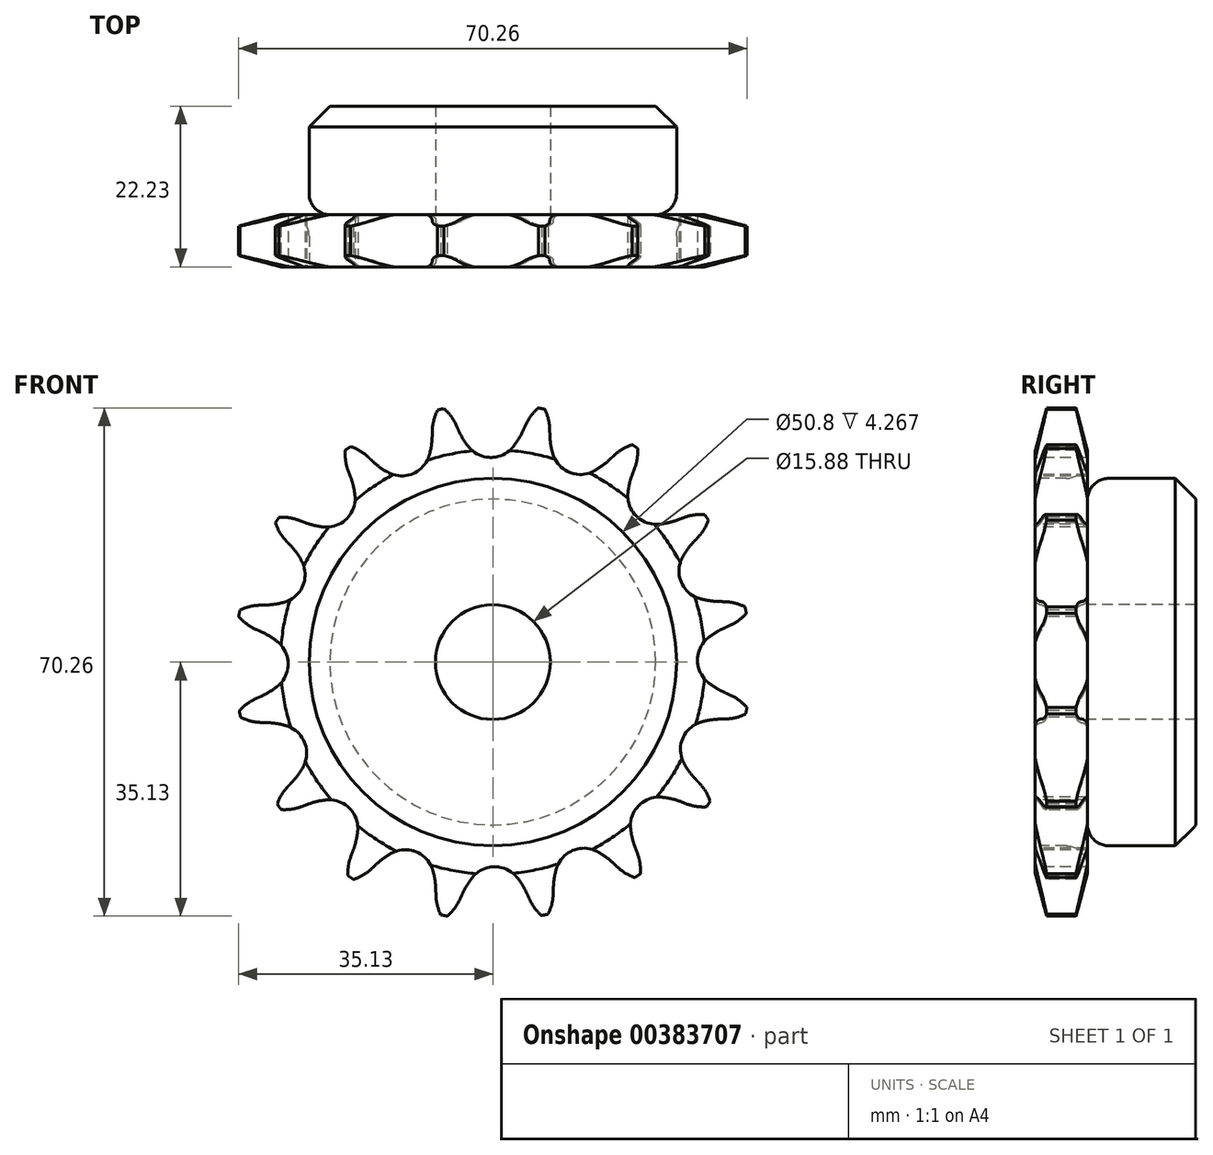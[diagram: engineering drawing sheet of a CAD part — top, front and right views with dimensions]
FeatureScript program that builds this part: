
annotation { "Feature Type Name" : "Feature", "Feature Type Description" : "" }
export const myFeature = defineFeature(function(context is Context, id is Id, definition is map)
    precondition{}
    {
        {
            var Q0;
            Q0=qCreatedBy(makeId("Right.planeOp"),FACE);
            var sketch = newSketch(context, id + "F0", { "sketchPlane" : qUnion([Q0])});
            skLineSegment(sketch, "E0", {"start": v(0, 0) * mm, "end": v(31.18, 0) * mm, "construction": true});
            skLineSegment(sketch, "E1.bottom", {"start": v(0, 7.94) * mm, "end": v(7.21, 7.94) * mm});
            skLineSegment(sketch, "E1.top", {"start": v(0, 35.69) * mm, "end": v(7.21, 35.69) * mm});
            skLineSegment(sketch, "E1.left", {"start": v(0, 7.94) * mm, "end": v(0, 35.69) * mm});
            skLineSegment(sketch, "E1.right", {"start": v(7.21, 7.94) * mm, "end": v(7.21, 35.69) * mm});
            skLineSegment(sketch, "E2.bottom", {"start": v(0, 7.94) * mm, "end": v(22.23, 7.94) * mm});
            skLineSegment(sketch, "E2.top", {"start": v(0, 25.4) * mm, "end": v(22.23, 25.4) * mm});
            skLineSegment(sketch, "E2.left", {"start": v(0, 7.94) * mm, "end": v(0, 25.4) * mm});
            skLineSegment(sketch, "E2.right", {"start": v(22.23, 7.94) * mm, "end": v(22.23, 25.4) * mm});
            skLineSegment(sketch, "E3.MirrorCS", {"start": v(7.21, -7.94) * mm, "end": v(7.21, -35.69) * mm});
            skLineSegment(sketch, "E4.MirrorCS", {"start": v(0, -7.94) * mm, "end": v(22.23, -7.94) * mm});
            skLineSegment(sketch, "E5.MirrorCS", {"start": v(0, -7.94) * mm, "end": v(0, -25.4) * mm});
            skLineSegment(sketch, "E6.MirrorCS", {"start": v(0, -7.94) * mm, "end": v(0, -35.69) * mm});
            skLineSegment(sketch, "E7.MirrorCS", {"start": v(22.23, -7.94) * mm, "end": v(22.23, -25.4) * mm});
            skLineSegment(sketch, "E8.MirrorCS", {"start": v(0, -25.4) * mm, "end": v(22.23, -25.4) * mm});
            skLineSegment(sketch, "E9.MirrorCS", {"start": v(0, -35.69) * mm, "end": v(7.21, -35.69) * mm});
            skSolve(sketch);
        }
        {
            var Q0;
            {var subQ5=sQuery(id+"F0.wireOp",EDGE,"E2.right");Q0=makeQuery(id+"F0.imprint","IMPRINT",FACE,{"disambiguationData":[TD([[makeQuery(id+"F0.imprint","IMPRINT",EDGE,{"derivedFrom":subQ5}),1.0]])]});}
            var Q1;
            {var subQ5=sQuery(id+"F0.wireOp",EDGE,"E2.left");Q1=makeQuery(id+"F0.imprint","IMPRINT",FACE,{"disambiguationData":[TD([[makeQuery(id+"F0.imprint","IMPRINT",EDGE,{"derivedFrom":subQ5}),-1.0]])]});}
            var Q2;
            {var subQ0=sQuery(id+"F0.wireOp",EDGE,"E1.top");Q2=makeQuery(id+"F0.imprint","IMPRINT",FACE,{"disambiguationData":[TD([[makeQuery(id+"F0.imprint","IMPRINT",EDGE,{"derivedFrom":subQ0}),-1.0]])]});}
            var Q3;
            Q3=sQuery(id+"F0.wireOp",EDGE,"E0");
            revolve(context, id + "F1", {"entities" : qUnion([Q0, Q1, Q2]), "axis" : qUnion([Q3]), "revolveType" : RevolveType.FULL});
        }
        {
            var Q0;
            Q0=makeQuery(id+"F1.opRevolve","SWEPT_EDGE",EDGE,{"disambiguationData":[OSD([sQuery(id+"F0.wireOp",EDGE,"E1.right"),sQuery(id+"F0.wireOp",EDGE,"E2.top")])]});
            fillet(context, id + "F2", {"entities" : qUnion([Q0]), "radius" : 2.95 * mm, "tangentPropagation" : true, "allowEdgeOverflow" : false});
        }
        {
            var Q0;
            Q0=makeQuery(id+"F1.opRevolve","SWEPT_EDGE",EDGE,{"disambiguationData":[OSD([sQuery(id+"F0.wireOp",EDGE,"E2.top"),sQuery(id+"F0.wireOp",EDGE,"E2.right")])]});
            chamfer(context, id + "F3", {"entities" : qUnion([Q0]), "width" : 2.87 * mm, "tangentPropagation" : true});
        }
        {
            var Q0;
            Q0=makeQuery(id+"F1.opRevolve","SWEPT_EDGE",EDGE,{"disambiguationData":[OSD([sQuery(id+"F0.wireOp",EDGE,"E1.top"),sQuery(id+"F0.wireOp",EDGE,"E1.left")])]});
            var Q1;
            Q1=makeQuery(id+"F1.opRevolve","SWEPT_FACE",FACE,{"disambiguationData":[OSD([sQuery(id+"F0.wireOp",EDGE,"E1.top")])]});
            chamfer(context, id + "F4", {"entities" : qUnion([Q0, Q1]), "chamferType" : ChamferType.TWO_OFFSETS, "width1" : 6.35 * mm, "oppositeDirection" : false, "width2" : 1.57 * mm, "tangentPropagation" : true});
        }
        {
            var Q0;
            Q0=qCreatedBy(makeId("Front.planeOp"),FACE);
            var sketch = newSketch(context, id + "F5", { "sketchPlane" : qUnion([Q0])});
            skCircle(sketch, "E10", {"center": v(0, -0.05) * mm, "radius": 32.55 * mm, "construction": true});
            skLineSegment(sketch, "E11", {"start": v(0, -0.05) * mm, "end": v(0, 32.5) * mm, "construction": true});
            skLineSegment(sketch, "E12", {"start": v(-32.56, -60.2) * mm, "end": v(-32.56, -60.2) * mm});
            skLineSegment(sketch, "E13", {"start": v(0, 32.5) * mm, "end": v(47.93, 32.5) * mm, "construction": true});
            skLineSegment(sketch, "E14", {"start": v(0, 32.5) * mm, "end": v(4.98, 36.5) * mm, "construction": true});
            skLineSegment(sketch, "E15", {"start": v(4.98, 36.5) * mm, "end": v(-4.46, 32.25) * mm, "construction": true});
            skLineSegment(sketch, "E16", {"start": v(-4.46, 32.25) * mm, "end": v(-4.46, 32.25) * mm});
            skLineSegment(sketch, "E17", {"start": v(0, -0.05) * mm, "end": v(-7.14, 35.8) * mm, "construction": true});
            skPoint(sketch, "E17.endSnap0", {"position": v(-6.06, 35.8) * mm});
            skLineSegment(sketch, "E18", {"start": v(-7.14, 35.8) * mm, "end": v(-7.14, 35.8) * mm});
            skLineSegment(sketch, "E19", {"start": v(-4.82, 33.05) * mm, "end": v(-4.82, 33.05) * mm});
            skArc(sketch, "E20", {"start": v(-4.5, 32.19) * mm, "mid": v(-4.65, 32.62) * mm, "end": v(-4.82, 33.05) * mm, "construction": true});
            skArc(sketch, "E21", {"start": v(-7.14, 35.8) * mm, "mid": v(-16.16, 26.46) * mm, "end": v(-4.5, 32.19) * mm, "construction": true});
            skArc(sketch, "E22", {"start": v(-10.19, 23.78) * mm, "mid": v(-5.13, 27.04) * mm, "end": v(-4.82, 33.05) * mm, "construction": true});
            skArc(sketch, "E23", {"start": v(-4.46, 32.25) * mm, "mid": v(-3.85, 31.1) * mm, "end": v(-3.1, 30.02) * mm});
            skLineSegment(sketch, "E24", {"start": v(-3.1, 30.02) * mm, "end": v(-3.1, 30.02) * mm});
            skLineSegment(sketch, "E25", {"start": v(-4.82, 33.05) * mm, "end": v(-7.66, 39.35) * mm, "construction": true});
            skLineSegment(sketch, "E26", {"start": v(-4.46, 32.25) * mm, "end": v(-4.82, 33.05) * mm, "construction": true});
            skLineSegment(sketch, "E27", {"start": v(-4.82, 33.05) * mm, "end": v(-4.46, 32.25) * mm});
            skArc(sketch, "E28.MirrorCS", {"start": v(4.45, 32.25) * mm, "mid": v(3.84, 31.1) * mm, "end": v(3.08, 30.02) * mm});
            skLineSegment(sketch, "E29.MirrorCS", {"start": v(4.45, 32.25) * mm, "end": v(4.8, 33.05) * mm});
            skArc(sketch, "E30", {"start": v(-3.1, 30.02) * mm, "mid": v(13.82, 41.92) * mm, "end": v(-4.46, 32.25) * mm, "construction": true});
            skArc(sketch, "E31", {"start": v(3.08, 30.02) * mm, "mid": v(0, 36.46) * mm, "end": v(-3.1, 30.02) * mm, "construction": true});
            skArc(sketch, "E32", {"start": v(-3.1, 30.02) * mm, "mid": v(0, 28.54) * mm, "end": v(3.08, 30.02) * mm});
            skArc(sketch, "E33", {"start": v(-4.82, 33.05) * mm, "mid": v(-5.79, 34.59) * mm, "end": v(-7.14, 35.8) * mm});
            skArc(sketch, "E34", {"start": v(-4.82, 33.05) * mm, "mid": v(-5.67, 34.43) * mm, "end": v(-6.82, 35.57) * mm});
            skArc(sketch, "E35", {"start": v(-6.82, 35.57) * mm, "mid": v(-6.98, 35.69) * mm, "end": v(-7.14, 35.8) * mm});
            skArc(sketch, "E36", {"start": v(-7.14, 35.8) * mm, "mid": v(-17.22, 31.96) * mm, "end": v(-10.19, 23.78) * mm, "construction": true});
            skArc(sketch, "E37.1.0", {"start": v(-27.44, -24.08) * mm, "mid": v(-19.07, -30.9) * mm, "end": v(-15.5, -20.71) * mm, "construction": true});
            skArc(sketch, "E37.1.1", {"start": v(-15.5, -20.71) * mm, "mid": v(-20.85, -17.96) * mm, "end": v(-26.2, -20.7) * mm, "construction": true});
            skArc(sketch, "E37.2.0", {"start": v(34.57, -11.72) * mm, "mid": v(36.3, -1.07) * mm, "end": v(25.7, -3.07) * mm, "construction": true});
            skArc(sketch, "E37.2.1", {"start": v(25.7, -3.07) * mm, "mid": v(25.98, -9.08) * mm, "end": v(31.03, -12.35) * mm, "construction": true});
            skPoint(sketch, "E37.center", {"position": v(0, 0) * mm});
            skArc(sketch, "E38.1.0", {"start": v(-26.2, -20.7) * mm, "mid": v(-26.99, -22.12) * mm, "end": v(-27.4, -23.7) * mm});
            skLineSegment(sketch, "E38.1.1", {"start": v(-26.2, -20.7) * mm, "end": v(-25.7, -20) * mm});
            skArc(sketch, "E38.1.2", {"start": v(-25.7, -20) * mm, "mid": v(-25, -18.88) * mm, "end": v(-24.45, -17.7) * mm});
            skArc(sketch, "E38.1.3", {"start": v(-24.45, -17.7) * mm, "mid": v(-24.71, -14.28) * mm, "end": v(-27.54, -12.34) * mm});
            skArc(sketch, "E38.2.0", {"start": v(31.03, -12.35) * mm, "mid": v(32.65, -12.31) * mm, "end": v(34.22, -11.88) * mm});
            skLineSegment(sketch, "E38.2.1", {"start": v(31.03, -12.35) * mm, "end": v(30.16, -12.26) * mm});
            skArc(sketch, "E38.2.2", {"start": v(30.16, -12.26) * mm, "mid": v(28.85, -12.21) * mm, "end": v(27.55, -12.33) * mm});
            skArc(sketch, "E38.2.3", {"start": v(27.55, -12.33) * mm, "mid": v(24.72, -14.26) * mm, "end": v(24.46, -17.68) * mm});
            skArc(sketch, "E39.MirrorCS", {"start": v(4.8, 33.05) * mm, "mid": v(5.65, 34.43) * mm, "end": v(6.8, 35.57) * mm});
            skArc(sketch, "E40.1.0", {"start": v(-17.14, 28.51) * mm, "mid": v(-18.45, 29.47) * mm, "end": v(-19.95, 30.08) * mm});
            skLineSegment(sketch, "E40.1.1", {"start": v(-17.14, 28.51) * mm, "end": v(-16.5, 27.91) * mm});
            skArc(sketch, "E40.1.2", {"start": v(-16.5, 27.91) * mm, "mid": v(-15.5, 27.08) * mm, "end": v(-14.4, 26.37) * mm});
            skArc(sketch, "E40.1.3", {"start": v(-14.4, 26.37) * mm, "mid": v(-10.97, 26.19) * mm, "end": v(-8.68, 28.74) * mm});
            skArc(sketch, "E40.1.4", {"start": v(-8.27, 31.32) * mm, "mid": v(-8.4, 30.02) * mm, "end": v(-8.68, 28.74) * mm});
            skArc(sketch, "E40.1.5", {"start": v(-8.24, 32.2) * mm, "mid": v(-8, 33.8) * mm, "end": v(-7.37, 35.3) * mm});
            skLineSegment(sketch, "E40.1.6", {"start": v(-8.27, 31.32) * mm, "end": v(-8.24, 32.2) * mm});
            skArc(sketch, "E40.2.0", {"start": v(-26.8, 19.6) * mm, "mid": v(-28.37, 19.99) * mm, "end": v(-29.99, 19.97) * mm});
            skLineSegment(sketch, "E40.2.1", {"start": v(-26.8, 19.6) * mm, "end": v(-25.97, 19.3) * mm});
            skArc(sketch, "E40.2.2", {"start": v(-25.97, 19.3) * mm, "mid": v(-24.72, 18.9) * mm, "end": v(-23.43, 18.68) * mm});
            skArc(sketch, "E40.2.3", {"start": v(-23.43, 18.68) * mm, "mid": v(-20.2, 19.82) * mm, "end": v(-19.06, 23.05) * mm});
            skArc(sketch, "E40.2.4", {"start": v(-19.67, 25.6) * mm, "mid": v(-19.28, 24.34) * mm, "end": v(-19.06, 23.05) * mm});
            skArc(sketch, "E40.2.5", {"start": v(-19.98, 26.41) * mm, "mid": v(-20.36, 27.99) * mm, "end": v(-20.35, 29.6) * mm});
            skLineSegment(sketch, "E40.2.6", {"start": v(-19.67, 25.6) * mm, "end": v(-19.98, 26.41) * mm});
            skArc(sketch, "E40.3.0", {"start": v(-32.3, 7.68) * mm, "mid": v(-33.9, 7.43) * mm, "end": v(-35.39, 6.8) * mm});
            skLineSegment(sketch, "E40.3.1", {"start": v(-32.3, 7.68) * mm, "end": v(-31.42, 7.7) * mm});
            skArc(sketch, "E40.3.2", {"start": v(-31.42, 7.7) * mm, "mid": v(-30.11, 7.83) * mm, "end": v(-28.84, 8.12) * mm});
            skArc(sketch, "E40.3.3", {"start": v(-28.84, 8.12) * mm, "mid": v(-26.28, 10.4) * mm, "end": v(-26.47, 13.83) * mm});
            skArc(sketch, "E40.3.4", {"start": v(-28, 15.94) * mm, "mid": v(-27.17, 14.93) * mm, "end": v(-26.47, 13.83) * mm});
            skArc(sketch, "E40.3.5", {"start": v(-28.6, 16.58) * mm, "mid": v(-29.56, 17.89) * mm, "end": v(-30.17, 19.4) * mm});
            skLineSegment(sketch, "E40.3.6", {"start": v(-28, 15.94) * mm, "end": v(-28.6, 16.58) * mm});
            skArc(sketch, "E40.4.0", {"start": v(-32.82, -5.44) * mm, "mid": v(-34.2, -6.28) * mm, "end": v(-35.34, -7.44) * mm});
            skLineSegment(sketch, "E40.4.1", {"start": v(-32.82, -5.44) * mm, "end": v(-32.02, -5.08) * mm});
            skArc(sketch, "E40.4.2", {"start": v(-32.02, -5.08) * mm, "mid": v(-30.86, -4.47) * mm, "end": v(-29.79, -3.71) * mm});
            skArc(sketch, "E40.4.3", {"start": v(-29.79, -3.71) * mm, "mid": v(-28.3, -0.62) * mm, "end": v(-29.79, 2.47) * mm});
            skArc(sketch, "E40.4.4", {"start": v(-32.02, 3.83) * mm, "mid": v(-30.86, 3.22) * mm, "end": v(-29.79, 2.47) * mm});
            skArc(sketch, "E40.4.5", {"start": v(-32.82, 4.2) * mm, "mid": v(-34.2, 5.04) * mm, "end": v(-35.34, 6.2) * mm});
            skLineSegment(sketch, "E40.4.6", {"start": v(-32.02, 3.83) * mm, "end": v(-32.82, 4.2) * mm});
            skArc(sketch, "E40.5.0", {"start": v(-28.28, -17.76) * mm, "mid": v(-29.23, -19.07) * mm, "end": v(-29.84, -20.57) * mm});
            skLineSegment(sketch, "E40.5.1", {"start": v(-28.28, -17.76) * mm, "end": v(-27.68, -17.12) * mm});
            skArc(sketch, "E40.5.2", {"start": v(-27.68, -17.12) * mm, "mid": v(-26.84, -16.11) * mm, "end": v(-26.14, -15) * mm});
            skArc(sketch, "E40.5.3", {"start": v(-26.14, -15) * mm, "mid": v(-25.95, -11.58) * mm, "end": v(-28.5, -9.3) * mm});
            skArc(sketch, "E40.5.4", {"start": v(-31.09, -8.89) * mm, "mid": v(-29.78, -9.01) * mm, "end": v(-28.5, -9.3) * mm});
            skArc(sketch, "E40.5.5", {"start": v(-31.96, -8.86) * mm, "mid": v(-33.57, -8.61) * mm, "end": v(-35.06, -7.98) * mm});
            skLineSegment(sketch, "E40.5.6", {"start": v(-31.09, -8.89) * mm, "end": v(-31.96, -8.86) * mm});
            skArc(sketch, "E40.6.0", {"start": v(-19.37, -27.4) * mm, "mid": v(-19.75, -28.98) * mm, "end": v(-19.74, -30.6) * mm});
            skLineSegment(sketch, "E40.6.1", {"start": v(-19.37, -27.4) * mm, "end": v(-19.06, -26.59) * mm});
            skArc(sketch, "E40.6.2", {"start": v(-19.06, -26.59) * mm, "mid": v(-18.67, -25.34) * mm, "end": v(-18.45, -24.04) * mm});
            skArc(sketch, "E40.6.3", {"start": v(-18.45, -24.04) * mm, "mid": v(-19.59, -20.81) * mm, "end": v(-22.82, -19.67) * mm});
            skArc(sketch, "E40.6.4", {"start": v(-25.36, -20.29) * mm, "mid": v(-24.1, -19.9) * mm, "end": v(-22.82, -19.67) * mm});
            skArc(sketch, "E40.6.5", {"start": v(-26.18, -20.6) * mm, "mid": v(-27.76, -20.98) * mm, "end": v(-29.38, -20.97) * mm});
            skLineSegment(sketch, "E40.6.6", {"start": v(-25.36, -20.29) * mm, "end": v(-26.18, -20.6) * mm});
            skArc(sketch, "E40.7.0", {"start": v(-7.45, -32.9) * mm, "mid": v(-7.2, -34.51) * mm, "end": v(-6.57, -36) * mm});
            skLineSegment(sketch, "E40.7.1", {"start": v(-7.45, -32.9) * mm, "end": v(-7.47, -32.03) * mm});
            skArc(sketch, "E40.7.2", {"start": v(-7.47, -32.03) * mm, "mid": v(-7.6, -30.73) * mm, "end": v(-7.88, -29.45) * mm});
            skArc(sketch, "E40.7.3", {"start": v(-7.88, -29.45) * mm, "mid": v(-10.17, -26.9) * mm, "end": v(-13.6, -27.09) * mm});
            skArc(sketch, "E40.7.4", {"start": v(-15.7, -28.62) * mm, "mid": v(-14.7, -27.79) * mm, "end": v(-13.6, -27.09) * mm});
            skArc(sketch, "E40.7.5", {"start": v(-16.35, -29.22) * mm, "mid": v(-17.66, -30.18) * mm, "end": v(-19.16, -30.79) * mm});
            skLineSegment(sketch, "E40.7.6", {"start": v(-15.7, -28.62) * mm, "end": v(-16.35, -29.22) * mm});
            skArc(sketch, "E40.8.0", {"start": v(5.67, -33.43) * mm, "mid": v(6.51, -34.82) * mm, "end": v(7.67, -35.95) * mm});
            skLineSegment(sketch, "E40.8.1", {"start": v(5.67, -33.43) * mm, "end": v(5.31, -32.63) * mm});
            skArc(sketch, "E40.8.2", {"start": v(5.31, -32.63) * mm, "mid": v(4.7, -31.48) * mm, "end": v(3.95, -30.4) * mm});
            skArc(sketch, "E40.8.3", {"start": v(3.95, -30.4) * mm, "mid": v(0.86, -28.92) * mm, "end": v(-2.23, -30.4) * mm});
            skArc(sketch, "E40.8.4", {"start": v(-3.6, -32.63) * mm, "mid": v(-2.99, -31.48) * mm, "end": v(-2.23, -30.4) * mm});
            skArc(sketch, "E40.8.5", {"start": v(-3.96, -33.43) * mm, "mid": v(-4.8, -34.82) * mm, "end": v(-5.96, -35.95) * mm});
            skLineSegment(sketch, "E40.8.6", {"start": v(-3.6, -32.63) * mm, "end": v(-3.96, -33.43) * mm});
            skArc(sketch, "E40.9.0", {"start": v(18, -28.9) * mm, "mid": v(19.3, -29.85) * mm, "end": v(20.8, -30.46) * mm});
            skLineSegment(sketch, "E40.9.1", {"start": v(18, -28.9) * mm, "end": v(17.36, -28.3) * mm});
            skArc(sketch, "E40.9.2", {"start": v(17.36, -28.3) * mm, "mid": v(16.35, -27.46) * mm, "end": v(15.24, -26.76) * mm});
            skArc(sketch, "E40.9.3", {"start": v(15.24, -26.76) * mm, "mid": v(11.82, -26.57) * mm, "end": v(9.53, -29.12) * mm});
            skArc(sketch, "E40.9.4", {"start": v(9.12, -31.7) * mm, "mid": v(9.24, -30.4) * mm, "end": v(9.53, -29.12) * mm});
            skArc(sketch, "E40.9.5", {"start": v(9.1, -32.58) * mm, "mid": v(8.85, -34.18) * mm, "end": v(8.21, -35.67) * mm});
            skLineSegment(sketch, "E40.9.6", {"start": v(9.12, -31.7) * mm, "end": v(9.1, -32.58) * mm});
            skArc(sketch, "E40.10.0", {"start": v(27.64, -19.99) * mm, "mid": v(29.21, -20.37) * mm, "end": v(30.83, -20.36) * mm});
            skLineSegment(sketch, "E40.10.1", {"start": v(27.64, -19.99) * mm, "end": v(26.82, -19.67) * mm});
            skArc(sketch, "E40.10.2", {"start": v(26.82, -19.67) * mm, "mid": v(25.57, -19.29) * mm, "end": v(24.28, -19.06) * mm});
            skArc(sketch, "E40.10.3", {"start": v(24.28, -19.06) * mm, "mid": v(21.04, -20.2) * mm, "end": v(19.9, -23.43) * mm});
            skArc(sketch, "E40.10.4", {"start": v(20.52, -25.98) * mm, "mid": v(20.13, -24.73) * mm, "end": v(19.9, -23.43) * mm});
            skArc(sketch, "E40.10.5", {"start": v(20.83, -26.8) * mm, "mid": v(21.21, -28.37) * mm, "end": v(21.2, -30) * mm});
            skLineSegment(sketch, "E40.10.6", {"start": v(20.52, -25.98) * mm, "end": v(20.83, -26.8) * mm});
            skArc(sketch, "E40.11.0", {"start": v(33.14, -8.06) * mm, "mid": v(34.74, -7.82) * mm, "end": v(36.24, -7.18) * mm});
            skLineSegment(sketch, "E40.11.1", {"start": v(33.14, -8.06) * mm, "end": v(32.27, -8.1) * mm});
            skArc(sketch, "E40.11.2", {"start": v(32.27, -8.1) * mm, "mid": v(30.96, -8.21) * mm, "end": v(29.68, -8.5) * mm});
            skArc(sketch, "E40.11.3", {"start": v(29.68, -8.5) * mm, "mid": v(27.13, -10.79) * mm, "end": v(27.32, -14.2) * mm});
            skArc(sketch, "E40.11.4", {"start": v(28.86, -16.33) * mm, "mid": v(28.02, -15.32) * mm, "end": v(27.32, -14.2) * mm});
            skArc(sketch, "E40.11.5", {"start": v(29.46, -16.96) * mm, "mid": v(30.41, -18.27) * mm, "end": v(31.02, -19.77) * mm});
            skLineSegment(sketch, "E40.11.6", {"start": v(28.86, -16.33) * mm, "end": v(29.46, -16.96) * mm});
            skArc(sketch, "E40.12.0", {"start": v(33.67, 5.06) * mm, "mid": v(35.05, 5.9) * mm, "end": v(36.19, 7.05) * mm});
            skLineSegment(sketch, "E40.12.1", {"start": v(33.67, 5.06) * mm, "end": v(32.87, 4.7) * mm});
            skArc(sketch, "E40.12.2", {"start": v(32.87, 4.7) * mm, "mid": v(31.7, 4.08) * mm, "end": v(30.64, 3.33) * mm});
            skArc(sketch, "E40.12.3", {"start": v(30.64, 3.33) * mm, "mid": v(29.15, 0.24) * mm, "end": v(30.64, -2.85) * mm});
            skArc(sketch, "E40.12.4", {"start": v(32.87, -4.22) * mm, "mid": v(31.7, -3.6) * mm, "end": v(30.64, -2.85) * mm});
            skArc(sketch, "E40.12.5", {"start": v(33.67, -4.58) * mm, "mid": v(35.05, -5.42) * mm, "end": v(36.19, -6.57) * mm});
            skLineSegment(sketch, "E40.12.6", {"start": v(32.87, -4.22) * mm, "end": v(33.67, -4.58) * mm});
            skArc(sketch, "E40.13.0", {"start": v(29.13, 17.38) * mm, "mid": v(30.08, 18.69) * mm, "end": v(30.7, 20.19) * mm});
            skLineSegment(sketch, "E40.13.1", {"start": v(29.13, 17.38) * mm, "end": v(28.53, 16.74) * mm});
            skArc(sketch, "E40.13.2", {"start": v(28.53, 16.74) * mm, "mid": v(27.7, 15.73) * mm, "end": v(26.99, 14.62) * mm});
            skArc(sketch, "E40.13.3", {"start": v(26.99, 14.62) * mm, "mid": v(26.8, 11.2) * mm, "end": v(29.35, 8.91) * mm});
            skArc(sketch, "E40.13.4", {"start": v(31.94, 8.5) * mm, "mid": v(30.63, 8.63) * mm, "end": v(29.35, 8.91) * mm});
            skArc(sketch, "E40.13.5", {"start": v(32.81, 8.48) * mm, "mid": v(34.41, 8.23) * mm, "end": v(35.9, 7.6) * mm});
            skLineSegment(sketch, "E40.13.6", {"start": v(31.94, 8.5) * mm, "end": v(32.81, 8.48) * mm});
            skArc(sketch, "E40.14.0", {"start": v(20.22, 27.02) * mm, "mid": v(20.6, 28.6) * mm, "end": v(20.59, 30.22) * mm});
            skLineSegment(sketch, "E40.14.1", {"start": v(20.22, 27.02) * mm, "end": v(19.9, 26.2) * mm});
            skArc(sketch, "E40.14.2", {"start": v(19.9, 26.2) * mm, "mid": v(19.52, 24.95) * mm, "end": v(19.3, 23.66) * mm});
            skArc(sketch, "E40.14.3", {"start": v(19.3, 23.66) * mm, "mid": v(20.43, 20.43) * mm, "end": v(23.67, 19.3) * mm});
            skArc(sketch, "E40.14.4", {"start": v(26.21, 19.9) * mm, "mid": v(24.96, 19.52) * mm, "end": v(23.67, 19.3) * mm});
            skArc(sketch, "E40.14.5", {"start": v(27.03, 20.21) * mm, "mid": v(28.6, 20.6) * mm, "end": v(30.22, 20.58) * mm});
            skLineSegment(sketch, "E40.14.6", {"start": v(26.21, 19.9) * mm, "end": v(27.03, 20.21) * mm});
            skArc(sketch, "E40.15.0", {"start": v(8.3, 32.53) * mm, "mid": v(8.05, 34.13) * mm, "end": v(7.42, 35.62) * mm});
            skLineSegment(sketch, "E40.15.1", {"start": v(8.3, 32.53) * mm, "end": v(8.32, 31.65) * mm});
            skArc(sketch, "E40.15.2", {"start": v(8.32, 31.65) * mm, "mid": v(8.45, 30.35) * mm, "end": v(8.73, 29.07) * mm});
            skArc(sketch, "E40.15.3", {"start": v(8.73, 29.07) * mm, "mid": v(11.02, 26.52) * mm, "end": v(14.44, 26.7) * mm});
            skArc(sketch, "E40.15.4", {"start": v(16.56, 28.24) * mm, "mid": v(15.55, 27.4) * mm, "end": v(14.44, 26.7) * mm});
            skArc(sketch, "E40.15.5", {"start": v(17.2, 28.84) * mm, "mid": v(18.5, 29.8) * mm, "end": v(20, 30.4) * mm});
            skLineSegment(sketch, "E40.15.6", {"start": v(16.56, 28.24) * mm, "end": v(17.2, 28.84) * mm});
            skPoint(sketch, "E40.center", {"position": v(0.42, -0.2) * mm});
            skLineSegment(sketch, "E41", {"start": v(-29.99, 19.97) * mm, "end": v(-25.92, 26.34) * mm});
            skLineSegment(sketch, "E42", {"start": v(-25.92, 26.34) * mm, "end": v(-20.35, 29.6) * mm});
            skSolve(sketch);
        }
        {
            var Q0;
            Q0=makeQuery(id+"F5.imprint","IMPRINT",FACE,{"disambiguationData":[TD([[makeQuery(id+"F5.imprint","IMPRINT",EDGE,{"derivedFrom":sQuery(id+"F5.wireOp",EDGE,"E40.2.0")}),-1.0]])]});
            extrude(context, id + "F6", {"entities" : qUnion([Q0]), "operationType" : NewBodyOperationType.REMOVE, "oppositeDirection" : true, "depth" : 25.4 * mm});
        }
        {
            var Q0;
            Q0=makeQuery(id+"F6.boolean.opBoolean","COPY",FACE,{"derivedFrom":makeQuery(id+"F6.opExtrude","SWEPT_FACE",FACE,{"disambiguationData":[OSD([sQuery(id+"F5.wireOp",EDGE,"E40.2.0")])]})});
            var Q1;
            Q1=makeQuery(id+"F6.boolean.opBoolean","COPY",FACE,{"derivedFrom":makeQuery(id+"F6.opExtrude","SWEPT_FACE",FACE,{"disambiguationData":[OSD([sQuery(id+"F5.wireOp",EDGE,"E40.2.1")])]})});
            var Q2;
            Q2=makeQuery(id+"F6.boolean.opBoolean","COPY",FACE,{"derivedFrom":makeQuery(id+"F6.opExtrude","SWEPT_FACE",FACE,{"disambiguationData":[OSD([sQuery(id+"F5.wireOp",EDGE,"E40.2.2")])]})});
            var Q3;
            Q3=makeQuery(id+"F6.boolean.opBoolean","COPY",FACE,{"derivedFrom":makeQuery(id+"F6.opExtrude","SWEPT_FACE",FACE,{"disambiguationData":[OSD([sQuery(id+"F5.wireOp",EDGE,"E40.2.3")])]})});
            var Q4;
            Q4=makeQuery(id+"F6.boolean.opBoolean","COPY",FACE,{"derivedFrom":makeQuery(id+"F6.opExtrude","SWEPT_FACE",FACE,{"disambiguationData":[OSD([sQuery(id+"F5.wireOp",EDGE,"E40.2.5")])]})});
            var Q5;
            Q5=makeQuery(id+"F6.boolean.opBoolean","COPY",FACE,{"derivedFrom":makeQuery(id+"F6.opExtrude","SWEPT_FACE",FACE,{"disambiguationData":[OSD([sQuery(id+"F5.wireOp",EDGE,"E40.2.4")])]})});
            var Q6;
            Q6=makeQuery(id+"F6.boolean.opBoolean","COPY",FACE,{"derivedFrom":makeQuery(id+"F6.opExtrude","SWEPT_FACE",FACE,{"disambiguationData":[OSD([sQuery(id+"F5.wireOp",EDGE,"E40.2.6")])]})});
            var Q7;
            Q7=makeQuery(id+"F1.opRevolve","SWEPT_FACE",FACE,{"disambiguationData":[OSD([sQuery(id+"F0.wireOp",EDGE,"E1.top")])]});
            circularPattern(context, id + "F7", {"patternType" : PatternType.FACE, "faces" : qUnion([Q0, Q1, Q2, Q3, Q4, Q5, Q6]), "axis" : qUnion([Q7]), "angle" : 360 * degree, "instanceCount" : 16, "equalSpace" : true});
        }
    });
